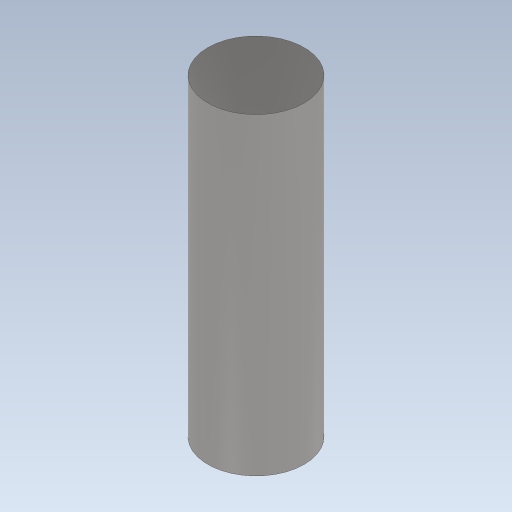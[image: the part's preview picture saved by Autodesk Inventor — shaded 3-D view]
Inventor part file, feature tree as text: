
AUTODESK INVENTOR PART (.ipt)
format: ipt  version: 2024.2 (Build 282272000, 272)  size: 89,088 bytes
history: native  units: in
note: dims shown in document units (in); Inventor stores cm internally (conversion verified against a paired STEP export)
features: extrude x1, sketch x1
ambient origin geometry x8: Origin, YZ Plane, XZ Plane, XY Plane, X Axis, Y Axis, Z Axis, Center Point
bodies: Solid1 (feature_tree)
feature tree (2):
  extrude  "Extrusion1"  Depth=1.0236in TaperAngle=0.0deg
  sketch  "Sketch1"  dims[d0=0.315in d1=1.0236in d2=0.0in]
